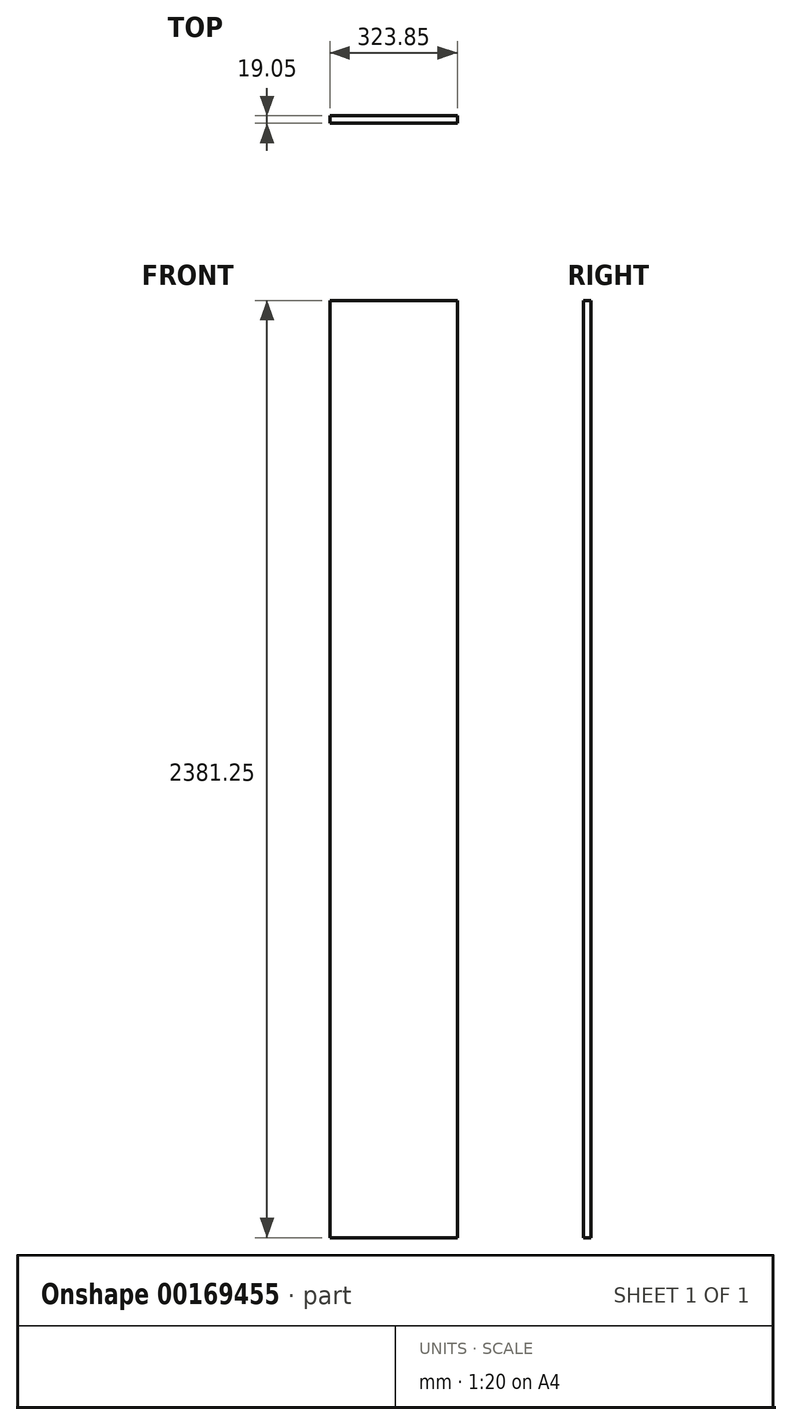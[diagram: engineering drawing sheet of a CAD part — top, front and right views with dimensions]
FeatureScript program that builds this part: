
annotation { "Feature Type Name" : "Feature", "Feature Type Description" : "" }
export const myFeature = defineFeature(function(context is Context, id is Id, definition is map)
    precondition{}
    {
        {
            var Q0;
            Q0=qCreatedBy(makeId("Front.planeOp"),FACE);
            var sketch = newSketch(context, id + "F0", { "sketchPlane" : qUnion([Q0])});
            skLineSegment(sketch, "E0.bottom", {"start": v(-199.45, 1569.12) * mm, "end": v(124.4, 1569.12) * mm});
            skLineSegment(sketch, "E0.top", {"start": v(-199.45, -812.13) * mm, "end": v(124.4, -812.13) * mm});
            skLineSegment(sketch, "E0.left", {"start": v(-199.45, 1569.12) * mm, "end": v(-199.45, -812.13) * mm});
            skLineSegment(sketch, "E0.right", {"start": v(124.4, 1569.12) * mm, "end": v(124.4, -812.13) * mm});
            skSolve(sketch);
        }
        {
            var Q0;
            Q0 = qSketchRegion(id + "F0", true);
            extrude(context, id + "F1", {"entities" : qUnion([Q0]), "depth" : 19.05 * mm});
        }
    });
